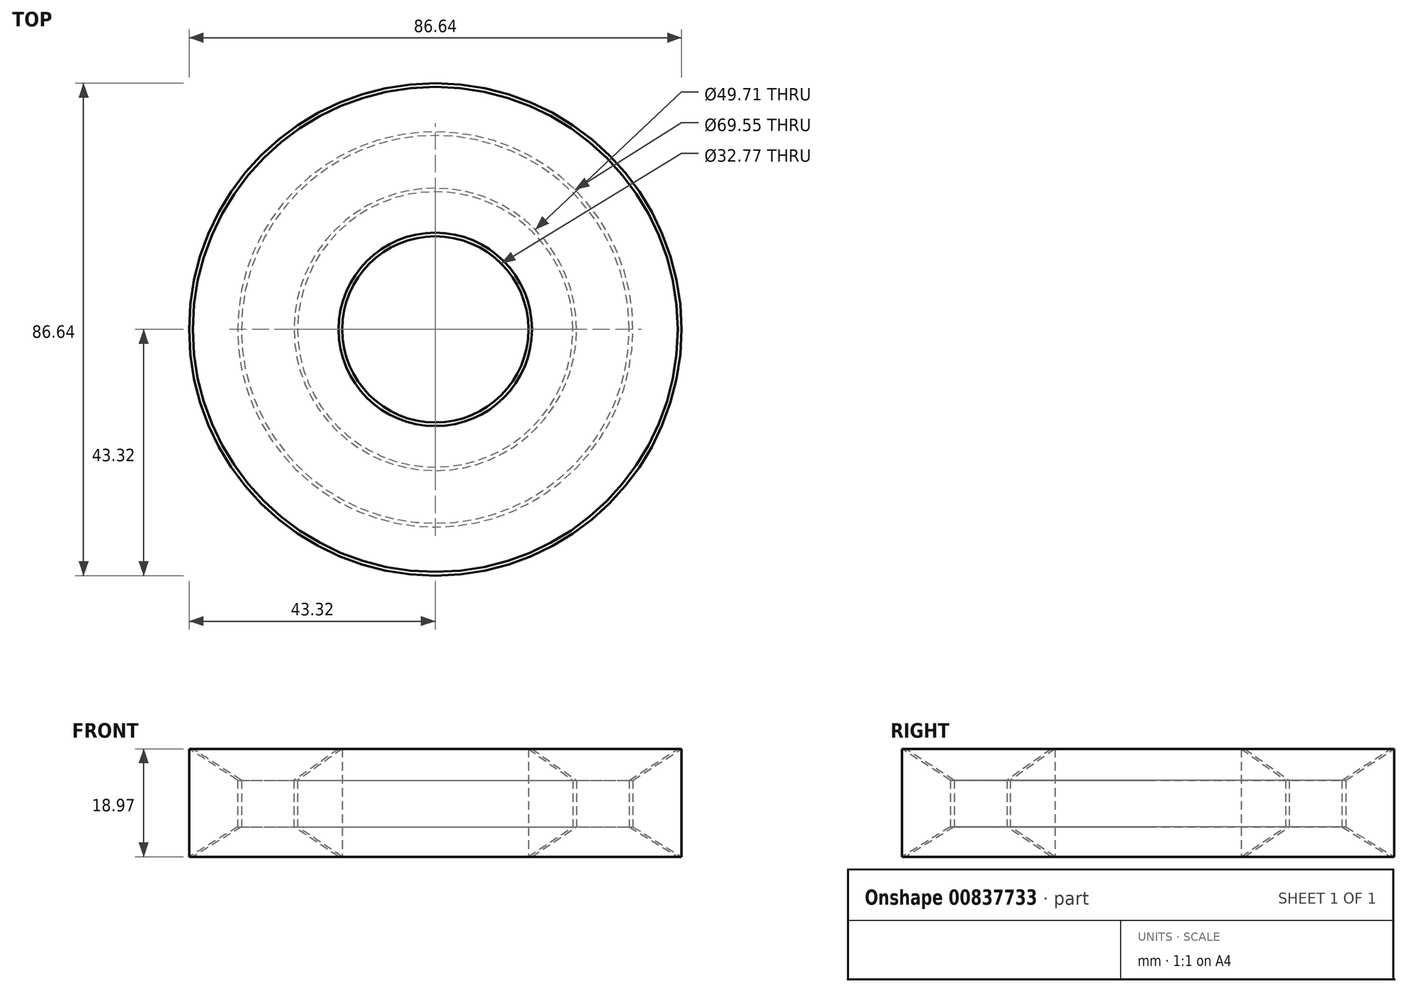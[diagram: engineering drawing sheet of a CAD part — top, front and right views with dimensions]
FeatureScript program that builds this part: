
annotation { "Feature Type Name" : "Feature", "Feature Type Description" : "" }
export const myFeature = defineFeature(function(context is Context, id is Id, definition is map)
    precondition{}
    {
        {
            var Q0;
            Q0=qCreatedBy(makeId("Right.planeOp"),FACE);
            var sketch = newSketch(context, id + "F0", { "sketchPlane" : qUnion([Q0])});
            skLineSegment(sketch, "E0", {"start": v(17.01, 0) * mm, "end": v(42.67, 0) * mm});
            skLineSegment(sketch, "E1", {"start": v(42.67, 18.97) * mm, "end": v(17.01, 18.97) * mm});
            skLineSegment(sketch, "E2", {"start": v(42.67, 18.97) * mm, "end": v(34.12, 13.45) * mm});
            skLineSegment(sketch, "E3", {"start": v(34.12, 13.45) * mm, "end": v(34.12, 5.26) * mm});
            skLineSegment(sketch, "E4", {"start": v(34.12, 5.26) * mm, "end": v(42.67, 0) * mm});
            skLineSegment(sketch, "E5", {"start": v(17.01, 18.97) * mm, "end": v(24.85, 13.45) * mm});
            skLineSegment(sketch, "E6", {"start": v(24.85, 13.45) * mm, "end": v(24.85, 5.26) * mm});
            skLineSegment(sketch, "E7", {"start": v(24.85, 5.26) * mm, "end": v(17.01, 0) * mm});
            skLineSegment(sketch, "E8", {"start": v(43.32, 18.97) * mm, "end": v(34.77, 13.45) * mm});
            skLineSegment(sketch, "E9", {"start": v(34.77, 13.45) * mm, "end": v(34.77, 5.26) * mm});
            skLineSegment(sketch, "E10", {"start": v(34.77, 5.26) * mm, "end": v(43.32, 0) * mm});
            skLineSegment(sketch, "E11", {"start": v(43.32, 0) * mm, "end": v(43.32, 18.97) * mm});
            skLineSegment(sketch, "E12", {"start": v(16.38, 18.97) * mm, "end": v(24.22, 13.45) * mm});
            skLineSegment(sketch, "E13", {"start": v(24.22, 13.45) * mm, "end": v(24.22, 5.26) * mm});
            skLineSegment(sketch, "E14", {"start": v(24.22, 5.26) * mm, "end": v(16.38, 0) * mm});
            skLineSegment(sketch, "E15", {"start": v(16.38, 0) * mm, "end": v(16.38, 18.97) * mm});
            skLineSegment(sketch, "E16", {"start": v(0, 0) * mm, "end": v(0, 10.57) * mm});
            skSolve(sketch);
        }
        {
            var Q0;
            Q0 = qSketchRegion(id + "F0", true);
            var Q1;
            Q1=sQuery(id+"F0.wireOp",EDGE,"E16");
            revolve(context, id + "F1", {"surfaceOperationType" : NewSurfaceOperationType.NEW, "entities" : qUnion([Q0]), "axis" : qUnion([Q1]), "revolveType" : RevolveType.FULL});
        }
    });
